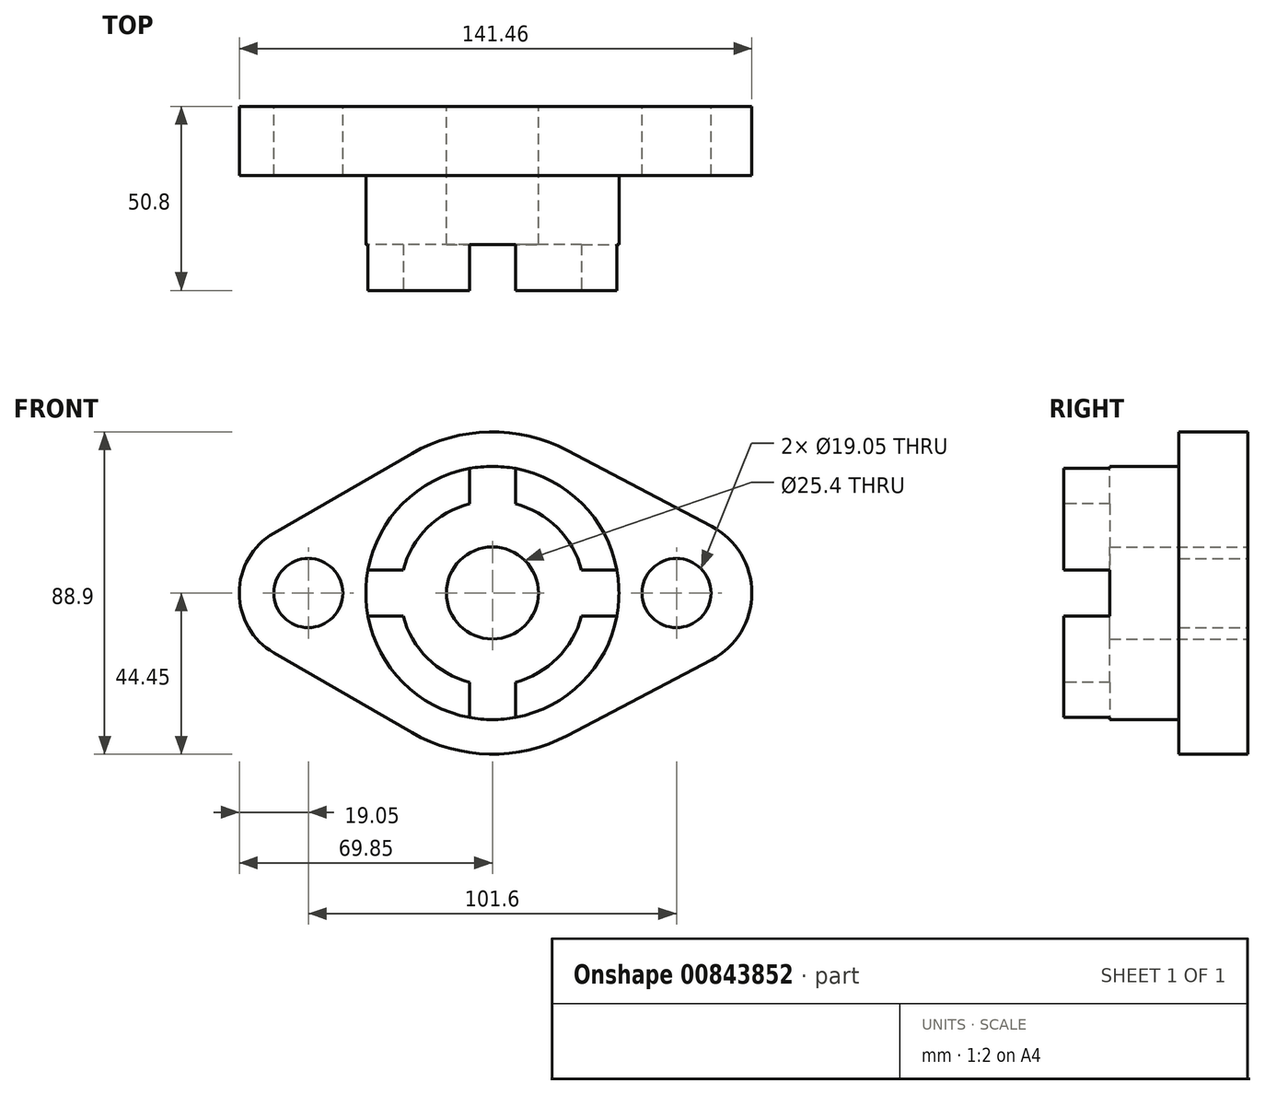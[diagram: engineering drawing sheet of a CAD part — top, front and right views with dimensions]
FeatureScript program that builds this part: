
annotation { "Feature Type Name" : "Feature", "Feature Type Description" : "" }
export const myFeature = defineFeature(function(context is Context, id is Id, definition is map)
    precondition{}
    {
        {
            var Q0;
            Q0=qCreatedBy(makeId("Front.planeOp"),FACE);
            var sketch = newSketch(context, id + "F0", { "sketchPlane" : qUnion([Q0])});
            skArc(sketch, "E0", {"start": v(-22.22, -38.5) * mm, "mid": v(-0.88, -44.44) * mm, "end": v(20.69, -39.34) * mm});
            skCircle(sketch, "E1", {"center": v(0, 0) * mm, "radius": 12.7 * mm});
            skCircle(sketch, "E2", {"center": v(-50.8, 0) * mm, "radius": 9.53 * mm});
            skCircle(sketch, "E3", {"center": v(50.8, 0) * mm, "radius": 9.53 * mm});
            skArc(sketch, "E4", {"start": v(-60.32, 16.5) * mm, "mid": v(-69.85, 0) * mm, "end": v(-60.33, -16.5) * mm});
            skArc(sketch, "E5", {"start": v(60.48, -18.42) * mm, "mid": v(71.6, 0) * mm, "end": v(60.48, 18.42) * mm});
            skLineSegment(sketch, "E6", {"start": v(-60.33, 16.5) * mm, "end": v(-22.23, 38.5) * mm});
            skLineSegment(sketch, "E7", {"start": v(-60.33, -16.5) * mm, "end": v(-22.22, -38.5) * mm});
            skLineSegment(sketch, "E8", {"start": v(60.48, 18.42) * mm, "end": v(20.69, 39.34) * mm});
            skLineSegment(sketch, "E9", {"start": v(60.48, -18.42) * mm, "end": v(20.69, -39.34) * mm});
            skArc(sketch, "E10.trimOffspring", {"start": v(20.69, 39.34) * mm, "mid": v(-0.88, 44.44) * mm, "end": v(-22.22, 38.5) * mm});
            skSolve(sketch);
        }
        {
            var Q0;
            Q0 = qSketchRegion(id + "F0", true);
            extrude(context, id + "F1", {"entities" : qUnion([Q0]), "depth" : 19.05 * mm, "offsetDistance" : 25.4 * mm});
        }
        {
            var Q0;
            Q0=makeQuery(id+"F1.opExtrude","CAP_FACE",FACE,{"disambiguationData":[OSD([sQuery(id+"F0.wireOp",EDGE,"E0"),sQuery(id+"F0.wireOp",EDGE,"E1"),sQuery(id+"F0.wireOp",EDGE,"E2"),sQuery(id+"F0.wireOp",EDGE,"E3"),sQuery(id+"F0.wireOp",EDGE,"E4"),sQuery(id+"F0.wireOp",EDGE,"E5"),sQuery(id+"F0.wireOp",EDGE,"E6"),sQuery(id+"F0.wireOp",EDGE,"E7"),sQuery(id+"F0.wireOp",EDGE,"E8"),sQuery(id+"F0.wireOp",EDGE,"E9"),sQuery(id+"F0.wireOp",EDGE,"E10.trimOffspring")])],"isStart":false});
            var sketch = newSketch(context, id + "F2", { "sketchPlane" : qUnion([Q0])});
            skCircle(sketch, "E11", {"center": v(0, 0) * mm, "radius": 34.93 * mm});
            skCircle(sketch, "E12", {"center": v(0, 0) * mm, "radius": 12.7 * mm});
            skSolve(sketch);
        }
        {
            var Q0;
            Q0 = qSketchRegion(id + "F2", true);
            extrude(context, id + "F3", {"entities" : qUnion([Q0]), "operationType" : NewBodyOperationType.ADD, "depth" : 19.05 * mm, "offsetDistance" : 25.4 * mm});
        }
        {
            var Q0;
            Q0=makeQuery(id+"F3.opExtrude","CAP_FACE",FACE,{"disambiguationData":[OSD([sQuery(id+"F2.wireOp",EDGE,"E11"),sQuery(id+"F2.wireOp",EDGE,"E12")])],"isStart":false});
            var sketch = newSketch(context, id + "F4", { "sketchPlane" : qUnion([Q0])});
            skCircle(sketch, "E13", {"center": v(0, 0) * mm, "radius": 34.93 * mm});
            skCircle(sketch, "E14", {"center": v(0, 0) * mm, "radius": 25.4 * mm});
            skSolve(sketch);
        }
        {
            var Q0;
            Q0 = qSketchRegion(id + "F4", true);
            extrude(context, id + "F5", {"entities" : qUnion([Q0]), "operationType" : NewBodyOperationType.ADD, "depth" : 12.7 * mm, "offsetDistance" : 25.4 * mm});
        }
        {
            var Q0;
            Q0=makeQuery(id+"F5.opExtrude","CAP_FACE",FACE,{"disambiguationData":[OSD([sQuery(id+"F4.wireOp",EDGE,"E13"),sQuery(id+"F4.wireOp",EDGE,"E14")])],"isStart":false});
            var sketch = newSketch(context, id + "F6", { "sketchPlane" : qUnion([Q0])});
            skLineSegment(sketch, "E15", {"start": v(-6.35, 24.6) * mm, "end": v(-6.35, 34.34) * mm});
            skLineSegment(sketch, "E16", {"start": v(6.35, 24.6) * mm, "end": v(6.35, 34.34) * mm});
            skLineSegment(sketch, "E17", {"start": v(24.6, 6.35) * mm, "end": v(34.34, 6.35) * mm});
            skLineSegment(sketch, "E18", {"start": v(24.6, -6.35) * mm, "end": v(34.34, -6.35) * mm});
            skLineSegment(sketch, "E19", {"start": v(6.35, -24.6) * mm, "end": v(6.35, -34.34) * mm});
            skLineSegment(sketch, "E20", {"start": v(-6.35, -24.6) * mm, "end": v(-6.35, -34.34) * mm});
            skLineSegment(sketch, "E21", {"start": v(-24.6, -6.35) * mm, "end": v(-34.34, -6.35) * mm});
            skLineSegment(sketch, "E22", {"start": v(-24.6, 6.35) * mm, "end": v(-34.34, 6.35) * mm});
            skArc(sketch, "E23", {"start": v(-34.34, 6.35) * mm, "mid": v(-34.92, 0) * mm, "end": v(-34.34, -6.35) * mm});
            skArc(sketch, "E24", {"start": v(-24.6, 6.35) * mm, "mid": v(-25.4, 0) * mm, "end": v(-24.6, -6.35) * mm});
            skArc(sketch, "E25.trimOffspring", {"start": v(-6.35, -24.6) * mm, "mid": v(0, -25.4) * mm, "end": v(6.35, -24.6) * mm});
            skArc(sketch, "E26.trimOffspring", {"start": v(-6.35, -34.34) * mm, "mid": v(0, -34.93) * mm, "end": v(6.35, -34.34) * mm});
            skArc(sketch, "E27.trimOffspring", {"start": v(24.6, -6.35) * mm, "mid": v(25.4, 0) * mm, "end": v(24.6, 6.35) * mm});
            skArc(sketch, "E28.trimOffspring", {"start": v(34.34, -6.35) * mm, "mid": v(34.93, 0) * mm, "end": v(34.34, 6.35) * mm});
            skArc(sketch, "E29.trimOffspring", {"start": v(6.35, 24.6) * mm, "mid": v(0, 25.4) * mm, "end": v(-6.35, 24.6) * mm});
            skArc(sketch, "E30.trimOffspring", {"start": v(6.35, 34.34) * mm, "mid": v(0, 34.92) * mm, "end": v(-6.35, 34.34) * mm});
            skSolve(sketch);
        }
        {
            var Q0;
            Q0 = qSketchRegion(id + "F6", true);
            extrude(context, id + "F7", {"entities" : qUnion([Q0]), "operationType" : NewBodyOperationType.REMOVE, "oppositeDirection" : true, "depth" : 12.7 * mm, "offsetDistance" : 25.4 * mm});
        }
    });
